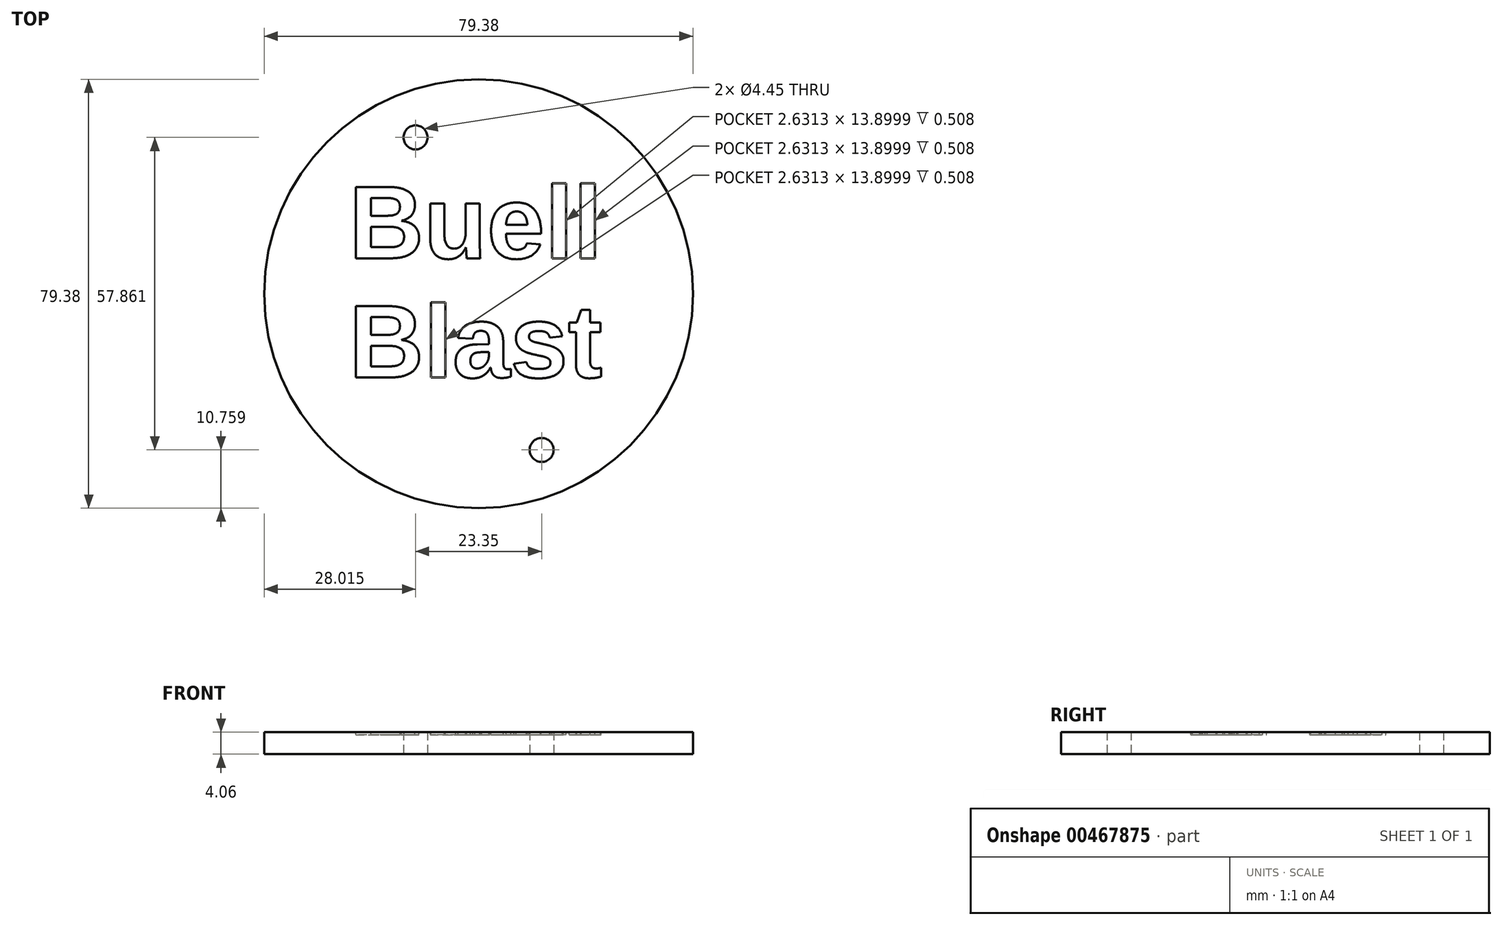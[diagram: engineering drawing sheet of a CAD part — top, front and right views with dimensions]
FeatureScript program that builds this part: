
annotation { "Feature Type Name" : "Feature", "Feature Type Description" : "" }
export const myFeature = defineFeature(function(context is Context, id is Id, definition is map)
    precondition{}
    {
        {
            var Q0;
            Q0=qCreatedBy(makeId("Top.planeOp"),FACE);
            var sketch = newSketch(context, id + "F0", { "sketchPlane" : qUnion([Q0])});
            skCircle(sketch, "E0", {"center": v(0, 0) * mm, "radius": 39.69 * mm});
            skPoint(sketch, "E1", {"position": v(0, 39.69) * mm});
            skCircle(sketch, "E2", {"center": v(-11.67, 28.93) * mm, "radius": 2.22 * mm});
            skCircle(sketch, "E3", {"center": v(11.67, -28.93) * mm, "radius": 2.22 * mm});
            skSolve(sketch);
        }
        {
            var Q0;
            Q0=makeQuery(id+"F0.imprint","IMPRINT",FACE,{"disambiguationData":[TD([[makeQuery(id+"F0.imprint","IMPRINT",EDGE,{"derivedFrom":sQuery(id+"F0.wireOp",EDGE,"E0")}),1.0]])]});
            extrude(context, id + "F1", {"entities" : qUnion([Q0]), "depth" : 4.06 * mm});
        }
        {
            var Q0;
            Q0=makeQuery(id+"F1.opExtrude","CAP_FACE",FACE,{"disambiguationData":[OSD([sQuery(id+"F0.wireOp",EDGE,"E0"),sQuery(id+"F0.wireOp",EDGE,"CIei4l1F-pO3S-ufCn-uWIM-jUZXUOuHnavh"),sQuery(id+"F0.wireOp",EDGE,"WXh1oEke-AvPH-Iuq8-7mBy-8Kstw0u6w3pi")])],"isStart":false});
            var sketch = newSketch(context, id + "F2", { "sketchPlane" : qUnion([Q0])});
            skText(sketch, "E4", { "text": "Buell\nBlast", "fontName": "Arimo-Bold.ttf"});
            const initialGuessF2  = {"E4": [-0.024, 0.00656, 1, 0, 0.01381]};
            skSetInitialGuess(sketch, initialGuessF2);
            skSolve(sketch);
        }
        {
            var Q0;
            Q0 = qSketchRegion(id + "F2", true);
            extrude(context, id + "F3", {"entities" : qUnion([Q0]), "operationType" : NewBodyOperationType.REMOVE, "oppositeDirection" : true, "depth" : 0.5 * mm});
        }
    });
